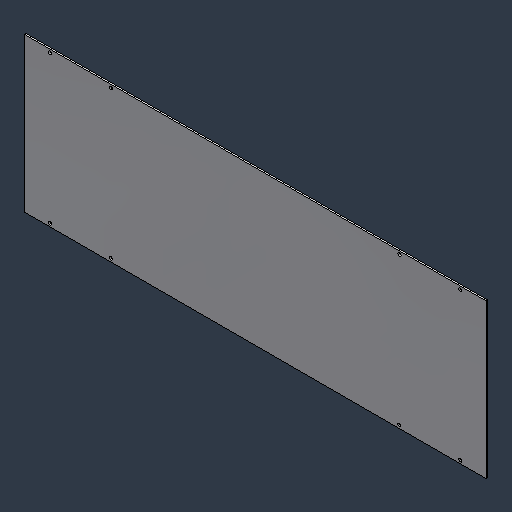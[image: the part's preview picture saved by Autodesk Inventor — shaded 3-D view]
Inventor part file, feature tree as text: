
AUTODESK INVENTOR PART (.ipt)
format: ipt  version: 2024.3 (Build 283343000, 343)  size: 86,528 bytes
history: native  units: mm (DEFAULTED — no unit token found)
features: mirror x1
ambient origin geometry x8: Origin, YZ Plane, XZ Plane, XY Plane, X Axis, Y Axis, Z Axis, Center Point
bodies: Solid1 (feature_tree)
feature tree (1):
  mirror  "Mirror1"
